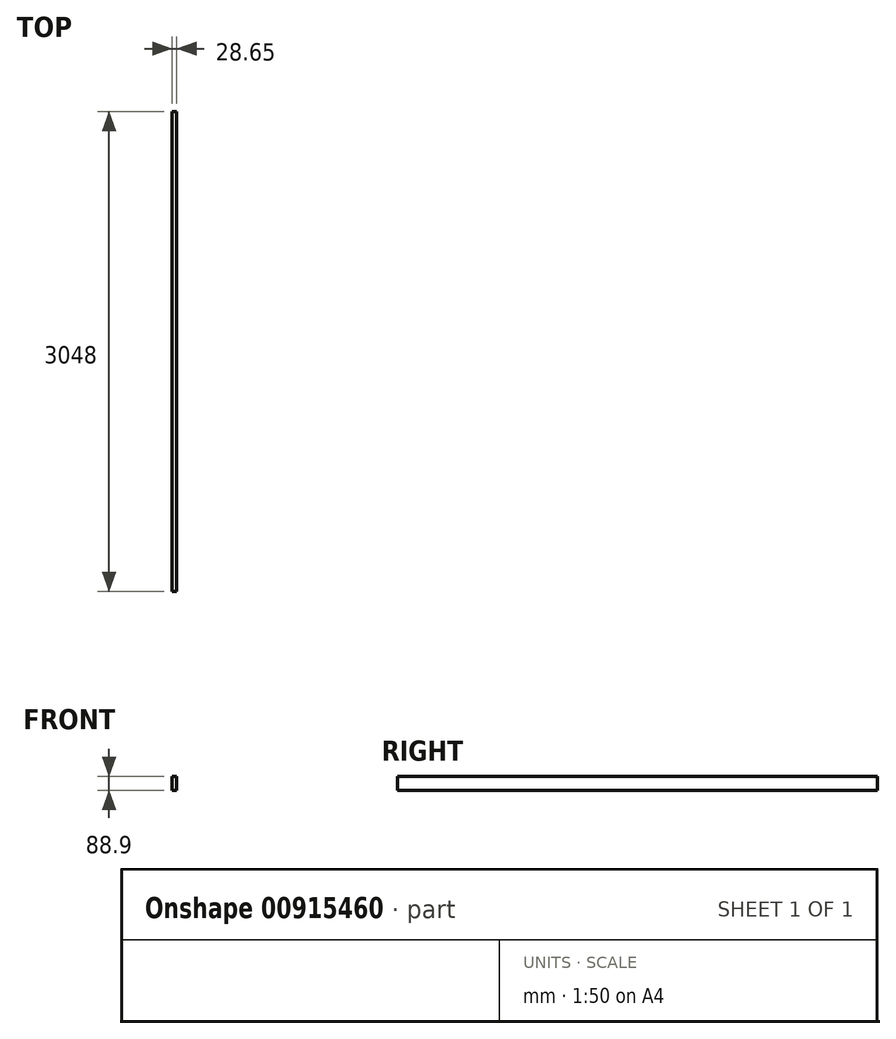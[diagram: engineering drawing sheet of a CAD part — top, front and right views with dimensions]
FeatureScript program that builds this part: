
annotation { "Feature Type Name" : "Feature", "Feature Type Description" : "" }
export const myFeature = defineFeature(function(context is Context, id is Id, definition is map)
    precondition{}
    {
        {
            var Q0;
            Q0=qCreatedBy(makeId("Front.planeOp"),FACE);
            var sketch = newSketch(context, id + "F0", { "sketchPlane" : qUnion([Q0])});
            skLineSegment(sketch, "E0.bottom", {"start": v(-15.49, 28.25) * mm, "end": v(13.16, 28.25) * mm});
            skLineSegment(sketch, "E0.top", {"start": v(-15.49, -60.65) * mm, "end": v(13.16, -60.65) * mm});
            skLineSegment(sketch, "E0.left", {"start": v(-15.49, 28.25) * mm, "end": v(-15.49, -60.65) * mm});
            skLineSegment(sketch, "E0.right", {"start": v(13.16, 28.25) * mm, "end": v(13.16, -60.65) * mm});
            skSolve(sketch);
        }
        {
            var Q0;
            Q0=makeQuery(id+"F0.imprint","IMPRINT",FACE,{"disambiguationData":[TD([[makeQuery(id+"F0.imprint","IMPRINT",EDGE,{"derivedFrom":sQuery(id+"F0.wireOp",EDGE,"E0.bottom")}),-1.0]])]});
            extrude(context, id + "F1", {"entities" : qUnion([Q0]), "depth" : 3048 * mm, "offsetDistance" : 25.4 * mm});
        }
    });
